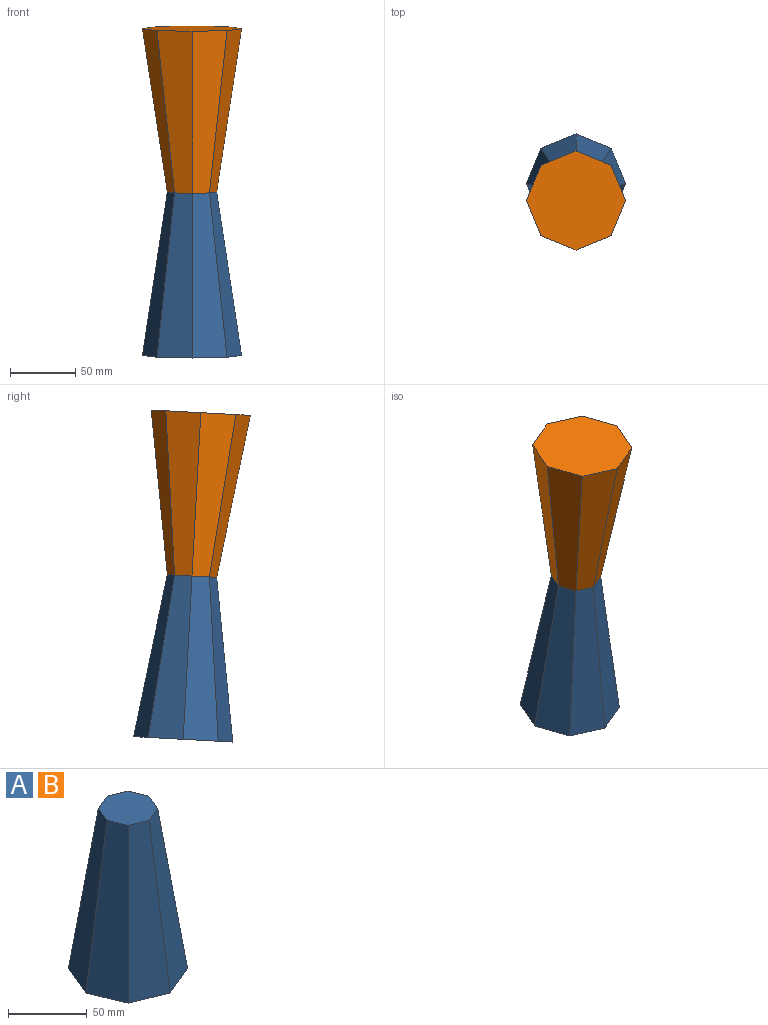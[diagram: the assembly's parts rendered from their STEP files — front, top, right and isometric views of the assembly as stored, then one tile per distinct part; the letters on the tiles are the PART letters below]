
ASSEMBLY  parts=2 mates=1
PART A: 10 faces, bbox 75.8x75.8x125 mm
  f0: plane 125x26.79mm, normal (0.38,0.91,0.14), area 2742.1mm2, adj f1,f7,f8,f9
  f1: plane 125x26.79mm, normal (-0.38,0.91,0.14), area 2742.1mm2, adj f0,f2,f8,f9
  f2: plane 125x26.79mm, normal (-0.91,0.38,0.14), area 2742.1mm2, adj f1,f3,f8,f9
  f3: plane 125x26.79mm, normal (-0.91,-0.38,0.14), area 2742.1mm2, adj f2,f4,f8,f9
  f4: plane 125x26.79mm, normal (-0.38,-0.91,0.14), area 2742.1mm2, adj f3,f5,f8,f9
  f5: plane 125x26.79mm, normal (0.38,-0.91,0.14), area 2742.1mm2, adj f4,f6,f8,f9
  f6: plane 125x26.79mm, normal (0.91,-0.38,0.14), area 2742.1mm2, adj f5,f7,f8,f9
  f7: plane 125x26.79mm, normal (0.91,0.38,0.14), area 2742.1mm2, adj f0,f6,f8,f9
  f8: plane 37.75x37.75mm, normal (0,0,1), area 1007.7mm2, adj f0,f1,f2,f3,f4,f5,f6,f7
  f9: plane 75.78x75.78mm, normal (0,0,-1), area 4060.7mm2, adj f0,f1,f2,f3,f4,f5,f6,f7
PART B: same geometry as A
PLACE A rot(axis=(1,0,0),3.1deg) t=(67.22,44.58,-1.27)mm
PLACE B rot(axis=(-1,0,0),176.9deg) t=(67.22,31.11,248.36)mm
MATE fastened A.f8 <-> B.f8  axis (0,-0.05,1) through (67.22,37.84,123.55)mm
